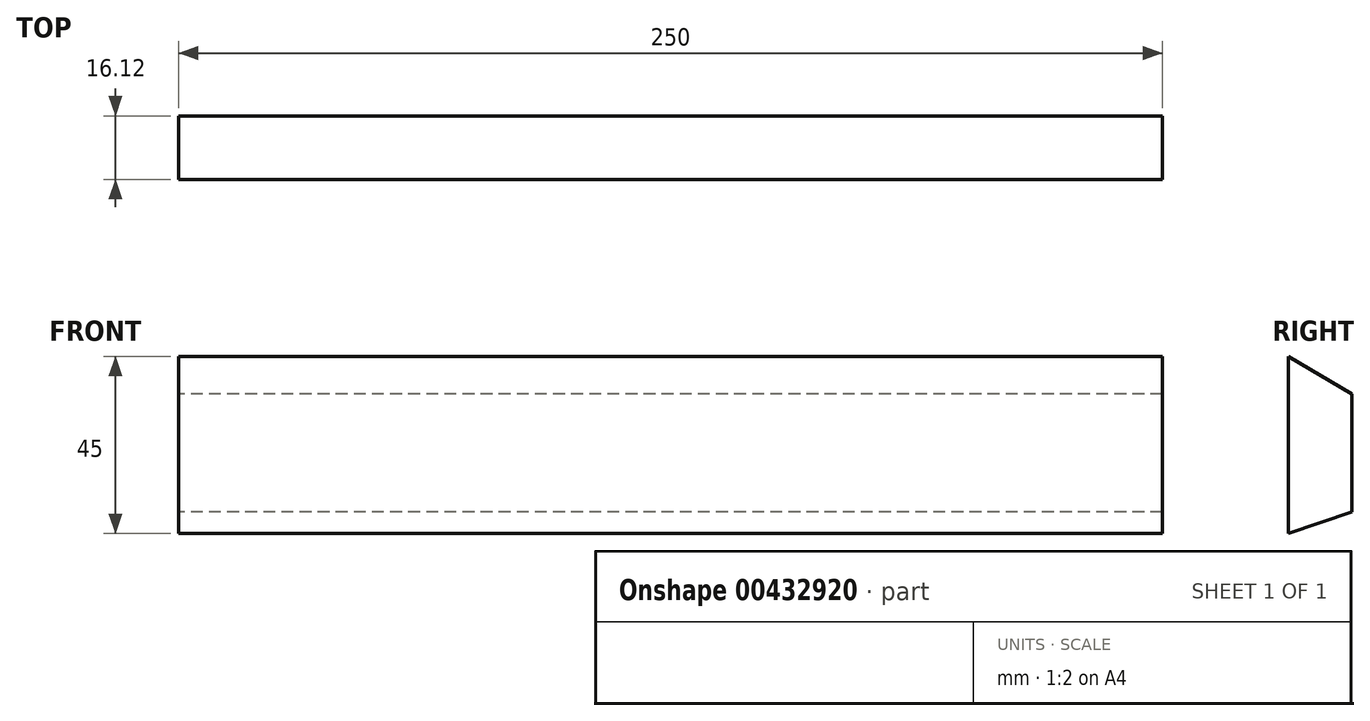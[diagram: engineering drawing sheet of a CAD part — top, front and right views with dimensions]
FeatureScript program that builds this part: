
annotation { "Feature Type Name" : "Feature", "Feature Type Description" : "" }
export const myFeature = defineFeature(function(context is Context, id is Id, definition is map)
    precondition{}
    {
        {
            var Q0;
            Q0=qCreatedBy(makeId("Right.planeOp"),FACE);
            var sketch = newSketch(context, id + "F0", { "sketchPlane" : qUnion([Q0])});
            skLineSegment(sketch, "E0", {"start": v(-9.46, 24.48) * mm, "end": v(-9.46, -20.52) * mm});
            skLineSegment(sketch, "E1", {"start": v(-9.46, -20.52) * mm, "end": v(6.66, -15) * mm});
            skLineSegment(sketch, "E2", {"start": v(6.66, -15) * mm, "end": v(6.66, 15) * mm});
            skLineSegment(sketch, "E3", {"start": v(6.66, 15) * mm, "end": v(-9.46, 24.48) * mm});
            skSolve(sketch);
        }
        {
            var Q0;
            Q0 = qSketchRegion(id + "F0", true);
            extrude(context, id + "F1", {"entities" : qUnion([Q0]), "depth" : 250 * mm});
        }
    });
